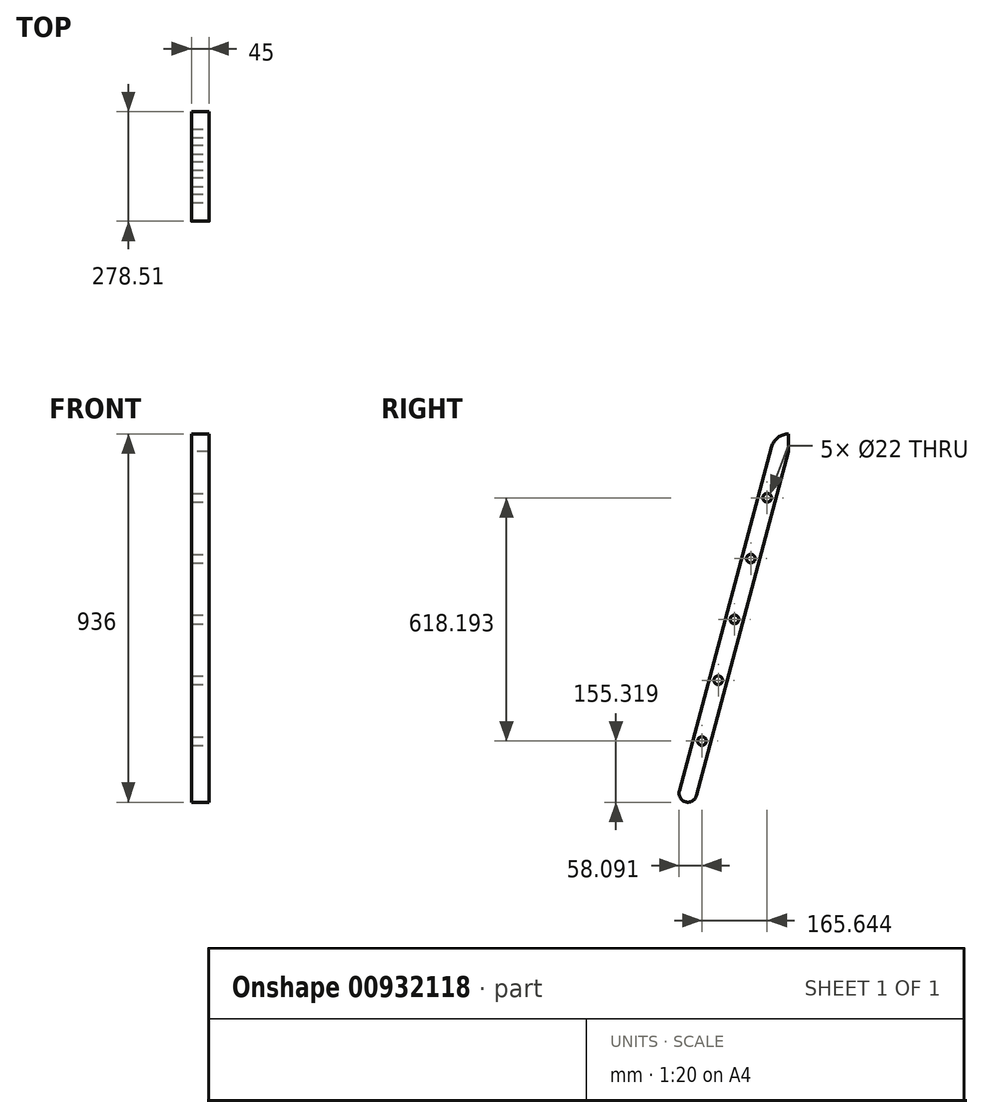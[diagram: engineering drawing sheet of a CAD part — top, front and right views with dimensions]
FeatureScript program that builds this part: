
annotation { "Feature Type Name" : "Feature", "Feature Type Description" : "" }
export const myFeature = defineFeature(function(context is Context, id is Id, definition is map)
    precondition{}
    {
        {
            var Q0;
            Q0=qCreatedBy(makeId("Right.planeOp"),FACE);
            var sketch = newSketch(context, id + "F0", { "sketchPlane" : qUnion([Q0])});
            skLineSegment(sketch, "E0", {"start": v(-90.87, 1417.76) * mm, "end": v(-325.14, 543.44) * mm});
            skLineSegment(sketch, "E1", {"start": v(-134.34, 1429.41) * mm, "end": v(-368.6, 555.09) * mm});
            skPoint(sketch, "E2.orphan", {"position": v(-329.61, 526.76) * mm});
            skLineSegment(sketch, "E3", {"start": v(-90.87, 1462.76) * mm, "end": v(-90.87, 526.76) * mm, "construction": true});
            skLineSegment(sketch, "E4", {"start": v(-90.87, 526.76) * mm, "end": v(-329.61, 526.76) * mm, "construction": true});
            skPoint(sketch, "E5.first.point", {"position": v(-244.47, 1018.38) * mm});
            skPoint(sketch, "E5.second.point", {"position": v(-202.5, 1001.17) * mm});
            skArc(sketch, "E6.filletArc", {"start": v(-90.87, 1462.76) * mm, "mid": v(-118.26, 1453.46) * mm, "end": v(-134.34, 1429.41) * mm});
            skLineSegment(sketch, "E7", {"start": v(-90.87, 1462.76) * mm, "end": v(-90.87, 1462.76) * mm});
            skLineSegment(sketch, "E8", {"start": v(-90.87, 1417.76) * mm, "end": v(-90.87, 1462.76) * mm});
            skLineSegment(sketch, "E9", {"start": v(-352.7, 527.53) * mm, "end": v(-352.7, 527.53) * mm});
            skPoint(sketch, "E10.visualSharp", {"position": v(-374.43, 533.35) * mm});
            skArc(sketch, "E10.filletArc", {"start": v(-368.6, 555.09) * mm, "mid": v(-366.36, 538.01) * mm, "end": v(-352.7, 527.53) * mm});
            skPoint(sketch, "E11.visualSharp", {"position": v(-330.97, 521.7) * mm});
            skArc(sketch, "E11.filletArc", {"start": v(-352.7, 527.53) * mm, "mid": v(-335.63, 529.78) * mm, "end": v(-325.14, 543.44) * mm});
            skSolve(sketch);
        }
        {
            var Q0;
            Q0=makeQuery(id+"F0.imprint","IMPRINT",FACE,{"disambiguationData":[TD([[makeQuery(id+"F0.imprint","IMPRINT",EDGE,{"derivedFrom":sQuery(id+"F0.wireOp",EDGE,"E0")}),-1.0]])]});
            extrude(context, id + "F1", {"entities" : qUnion([Q0]), "depth" : 45 * mm, "offsetDistance" : 25 * mm});
        }
        {
            var Q0;
            Q0=makeQuery(id+"F1.opExtrude","CAP_FACE",FACE,{"disambiguationData":[OSD([sQuery(id+"F0.wireOp",EDGE,"E0"),sQuery(id+"F0.wireOp",EDGE,"E1"),sQuery(id+"F0.wireOp",EDGE,"E6.filletArc"),sQuery(id+"F0.wireOp",EDGE,"E8"),sQuery(id+"F0.wireOp",EDGE,"E10.filletArc"),sQuery(id+"F0.wireOp",EDGE,"E11.filletArc")])],"isStart":false});
            var sketch = newSketch(context, id + "F2", { "sketchPlane" : qUnion([Q0])});
            skArc(sketch, "E12.0", {"start": v(-90.87, 1462.76) * mm, "mid": v(-118.26, 1453.46) * mm, "end": v(-134.34, 1429.41) * mm});
            skLineSegment(sketch, "E13.0", {"start": v(-134.34, 1429.41) * mm, "end": v(-368.6, 555.09) * mm});
            skLineSegment(sketch, "E14.0", {"start": v(-90.87, 1417.76) * mm, "end": v(-325.14, 543.44) * mm});
            skLineSegment(sketch, "E15.0", {"start": v(-90.87, 1417.76) * mm, "end": v(-90.87, 1462.76) * mm});
            skArc(sketch, "E16.0", {"start": v(-368.6, 555.09) * mm, "mid": v(-352.7, 527.53) * mm, "end": v(-325.14, 543.44) * mm});
            skLineSegment(sketch, "E17.0", {"start": v(-112.6, 1423.59) * mm, "end": v(-346.88, 549.26) * mm, "construction": true});
            skPoint(sketch, "E18", {"position": v(-311.29, 682.08) * mm});
            skPoint(sketch, "E19", {"position": v(-269.88, 836.63) * mm});
            skPoint(sketch, "E20", {"position": v(-228.47, 991.18) * mm});
            skPoint(sketch, "E21", {"position": v(-187.06, 1145.72) * mm});
            skPoint(sketch, "E22", {"position": v(-145.64, 1300.27) * mm});
            skSolve(sketch);
        }
        {
            var Q0;
            Q0=sQuery(id+"F2.wireOp",VERTEX,"E22");
            var Q1;
            Q1=sQuery(id+"F2.wireOp",VERTEX,"E21");
            var Q2;
            Q2=sQuery(id+"F2.wireOp",VERTEX,"E20");
            var Q3;
            Q3=sQuery(id+"F2.wireOp",VERTEX,"E19");
            var Q4;
            Q4=sQuery(id+"F2.wireOp",VERTEX,"E18");
            var Q5;
            Q5=makeQuery(id+"F1.opExtrude","SWEPT_BODY",BODY,{"disambiguationData":[OSD([sQuery(id+"F0.wireOp",EDGE,"E0"),sQuery(id+"F0.wireOp",EDGE,"E1"),sQuery(id+"F0.wireOp",EDGE,"E6.filletArc"),sQuery(id+"F0.wireOp",EDGE,"E8"),sQuery(id+"F0.wireOp",EDGE,"E10.filletArc"),sQuery(id+"F0.wireOp",EDGE,"E11.filletArc")])]});
            hole(context, id + "F3", {"style" : HoleStyle.SIMPLE, "endStyle" : HoleEndStyle.THROUGH, "holeDiameter" : 22 * mm, "majorDiameter" : 5 * mm, "isTappedThrough" : true, "tappedDepth" : 12 * mm, "tapClearance" : 3, "startFromSketch" : true, "locations" : qUnion([Q0, Q1, Q2, Q3, Q4]), "scope" : qUnion([Q5])});
        }
    });
